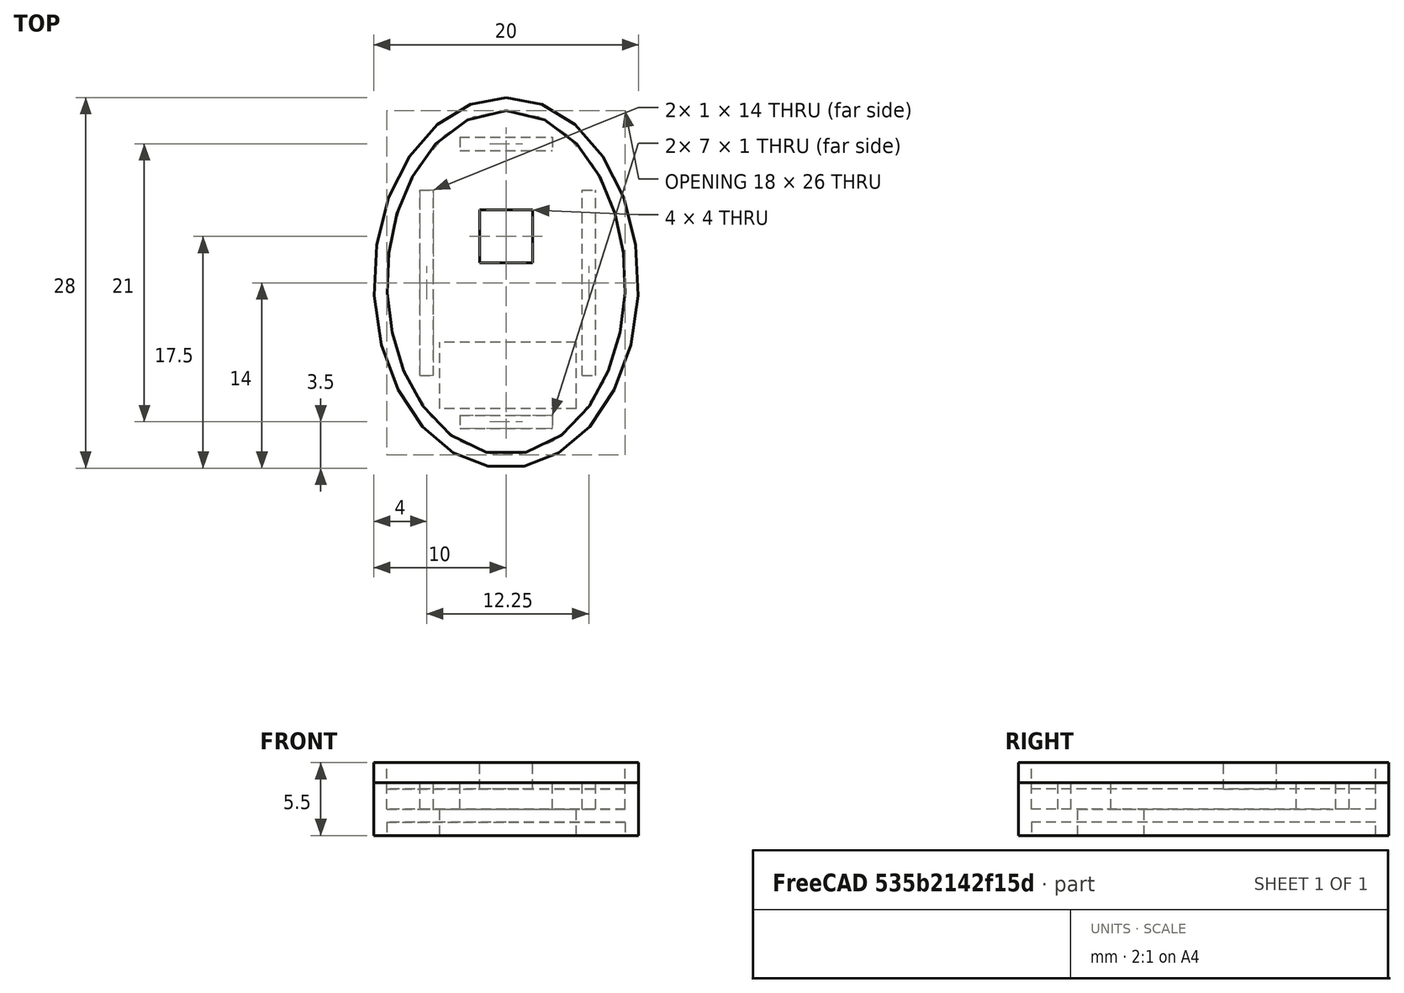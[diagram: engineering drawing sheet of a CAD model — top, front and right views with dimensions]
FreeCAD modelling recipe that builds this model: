
FCSTD DOCUMENT  (FreeCAD 0.18.1R)
Label: UVSensorEnclosure
License: All rights reserved
LicenseURL: http://en.wikipedia.org/wiki/All_rights_reserved
objects: Part::Box×7, Part::Extrusion×5, Part::Ellipse×4, Part::Cut×3, Part::MultiFuse×3
note: 22 computed .brp shape members not serialized (recipe doc carries the construction recipe); baked Part::Feature solids carry a one-line shape summary decoded from their .brp

FEATURE [Part::Box] Box  label="Cube"
  AttacherType = Attacher::AttachEngine3D
  Height = 1
  Length = 10.3
  Placement = pos=(-5,-9.5,5) rot=(0,0,1;0rad)
  Width = 19.3
FEATURE [Part::Ellipse] Ellipse
  Angle0 = 0
  Angle1 = 360
  AttacherType = Attacher::AttachEngine3D
  MajorRadius = 14
  MinorRadius = 10
  Placement = pos=(0,0,0) rot=(0,0,1;1.5708rad)
FEATURE [Part::Ellipse] Ellipse001
  Angle0 = 0
  Angle1 = 360
  AttacherType = Attacher::AttachEngine3D
  MajorRadius = 13
  MinorRadius = 9
  Placement = pos=(0,0,0) rot=(0,0,1;1.5708rad)
FEATURE [Part::Extrusion] Extrude
  Base = -> Ellipse001
  Dir = (0,0,1)
  DirMode = 2
  FaceMakerClass = Part::FaceMakerBullseye
  LengthFwd = 5
  LengthRev = 0
  Placement = pos=(0,0,2) rot=(0,0,1;0rad)
  Solid = true
  Symmetric = false
FEATURE [Part::Extrusion] Extrude001
  Base = -> Ellipse
  Dir = (0,0,1)
  DirMode = 2
  FaceMakerClass = Part::FaceMakerBullseye
  LengthFwd = 5.5
  LengthRev = 0
  Solid = true
  Symmetric = false
FEATURE [Part::Cut] Cut
  Base = -> Extrude001
  Tool = -> Extrude
FEATURE [Part::Box] Box001  label="Cube001"
  AttacherType = Attacher::AttachEngine3D
  Height = 3
  Length = 4
  Placement = pos=(-2,1.5,6) rot=(0,0,1;0rad)
  Width = 4
FEATURE [Part::Box] Box002  label="Cube002"
  AttacherType = Attacher::AttachEngine3D
  Height = 12
  Length = 10.3
  Placement = pos=(-5,-9.5,-7) rot=(0,0,1;0rad)
  Width = 5
FEATURE [Part::Box] Box003  label="Cube003"
  AttacherType = Attacher::AttachEngine3D
  Height = 4
  Length = 7
  Placement = pos=(-3.5,10,0) rot=(0,0,1;0rad)
  Width = 1
FEATURE [Part::Box] Box004  label="Cube004"
  AttacherType = Attacher::AttachEngine3D
  Height = 4
  Length = 7
  Placement = pos=(-3.5,-11,0) rot=(0,0,1;0rad)
  Width = 1
FEATURE [Part::MultiFuse] Fusion  label=" Fusion - sensor"
  Placement = pos=(0,0,-3) rot=(0,0,1;0rad)
  Shapes = -> [Box001,Box,Box002]
FEATURE [Part::Box] Box005  label="Cube005"
  AttacherType = Attacher::AttachEngine3D
  Height = 4
  Length = 14
  Placement = pos=(-5.5,-7,0) rot=(0,0,1;1.5708rad)
  Width = 1
FEATURE [Part::Box] Box006  label="Cube006"
  AttacherType = Attacher::AttachEngine3D
  Height = 4
  Length = 14
  Placement = pos=(6.75,-7,0) rot=(0,0,1;1.5708rad)
  Width = 1
FEATURE [Part::MultiFuse] Fusion001  label="Fusion - base"
  Shapes = -> [Box003,Box004,Box005,Box006,Cut]
FEATURE [Part::Cut] Cut001  label="UVSensorBase"
  Base = -> Fusion001
  Tool = -> Fusion
FEATURE [Part::Ellipse] Ellipse002
  Angle0 = 0
  Angle1 = 360
  AttacherType = Attacher::AttachEngine3D
  MajorRadius = 14
  MinorRadius = 10
  Placement = pos=(0,0,0) rot=(0,0,1;1.5708rad)
FEATURE [Part::Ellipse] Ellipse003
  Angle0 = 0
  Angle1 = 360
  AttacherType = Attacher::AttachEngine3D
  MajorRadius = 13
  MinorRadius = 9
  Placement = pos=(0,0,0) rot=(0,0,1;1.5708rad)
FEATURE [Part::Extrusion] Extrude002
  Base = -> Ellipse002
  Dir = (0,0,1)
  DirMode = 2
  FaceMakerClass = Part::FaceMakerBullseye
  LengthFwd = 1.5
  LengthRev = 0
  Placement = pos=(0,0,4) rot=(0,0,1;0rad)
  Solid = true
  Symmetric = false
FEATURE [Part::Extrusion] Extrude003
  Base = -> Ellipse003
  Dir = (0,0,1)
  DirMode = 2
  FaceMakerClass = Part::FaceMakerBullseye
  LengthFwd = 1
  LengthRev = 0
  Solid = true
  Symmetric = false
FEATURE [Part::Extrusion] Extrude004
  Base = -> Ellipse003
  Dir = (0,0,1)
  DirMode = 2
  FaceMakerClass = Part::FaceMakerBullseye
  LengthFwd = 1.2
  LengthRev = 0
  Placement = pos=(0,0,3.5) rot=(0,0,1;0rad)
  Solid = true
  Symmetric = false
FEATURE [Part::MultiFuse] Fusion002
  Shapes = -> [Extrude004,Extrude002]
FEATURE [Part::Cut] Cut002
  Base = -> Fusion002
  Tool = -> Fusion
